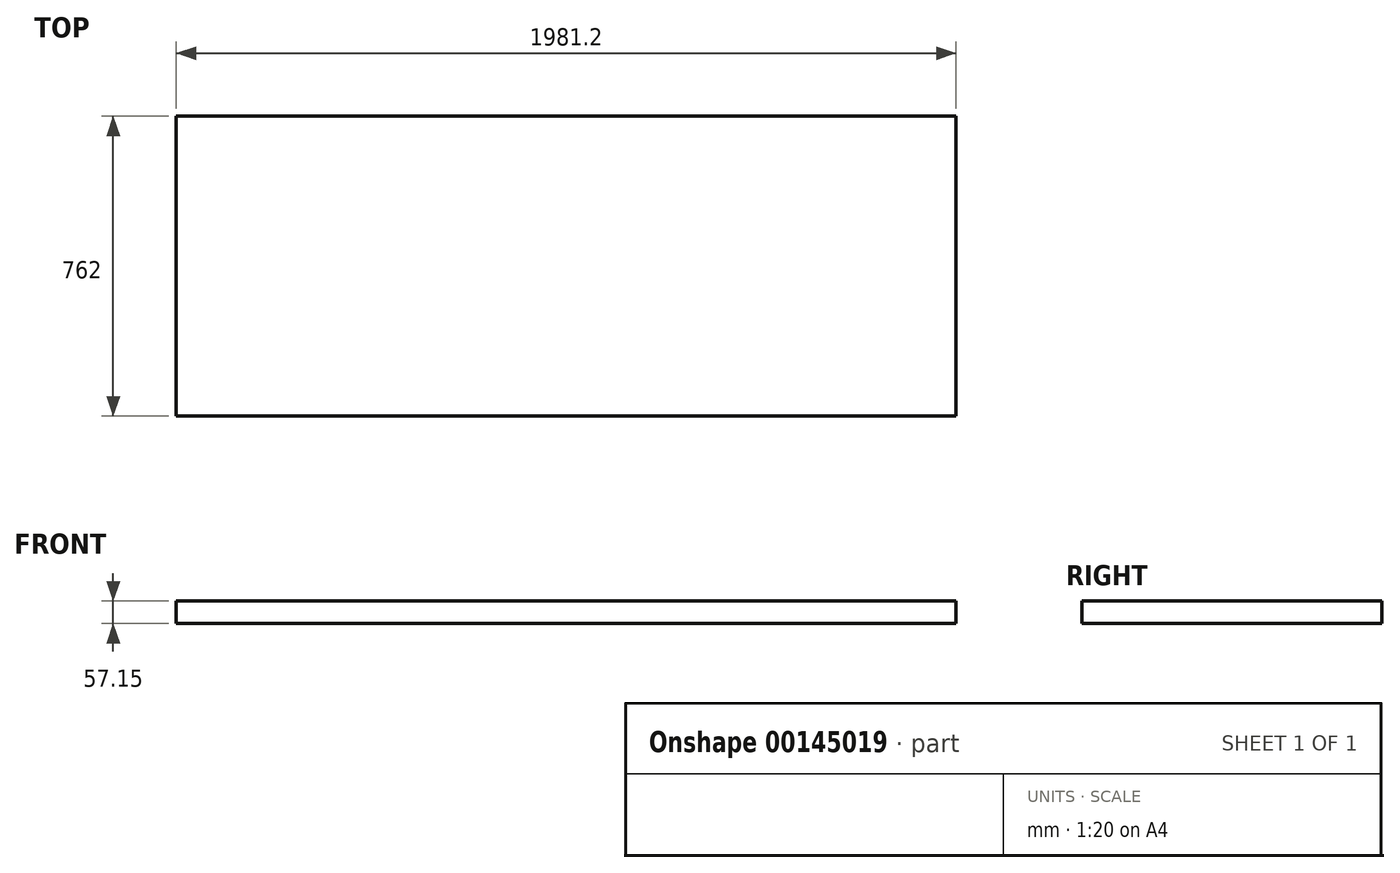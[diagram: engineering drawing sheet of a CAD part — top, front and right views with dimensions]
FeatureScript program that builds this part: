
annotation { "Feature Type Name" : "Feature", "Feature Type Description" : "" }
export const myFeature = defineFeature(function(context is Context, id is Id, definition is map)
    precondition{}
    {
        {
            var Q0;
            Q0=qCreatedBy(makeId("Top.planeOp"),FACE);
            var sketch = newSketch(context, id + "F0", { "sketchPlane" : qUnion([Q0])});
            skLineSegment(sketch, "E0.bottom", {"start": v(-251.38, 377.85) * mm, "end": v(1729.82, 377.85) * mm});
            skLineSegment(sketch, "E0.top", {"start": v(-251.38, -384.15) * mm, "end": v(1729.82, -384.15) * mm});
            skLineSegment(sketch, "E0.right", {"start": v(1729.82, 377.85) * mm, "end": v(1729.82, -384.15) * mm});
            skLineSegment(sketch, "E1", {"start": v(-251.38, 377.85) * mm, "end": v(-251.38, -384.15) * mm});
            skSolve(sketch);
        }
        {
            var Q0;
            Q0=makeQuery(id+"F0.imprint","IMPRINT",FACE,{"disambiguationData":[TD([[makeQuery(id+"F0.imprint","IMPRINT",EDGE,{"derivedFrom":sQuery(id+"F0.wireOp",EDGE,"E0.bottom")}),-1.0]])]});
            extrude(context, id + "F1", {"entities" : qUnion([Q0]), "depth" : 57.15 * mm});
        }
    });
